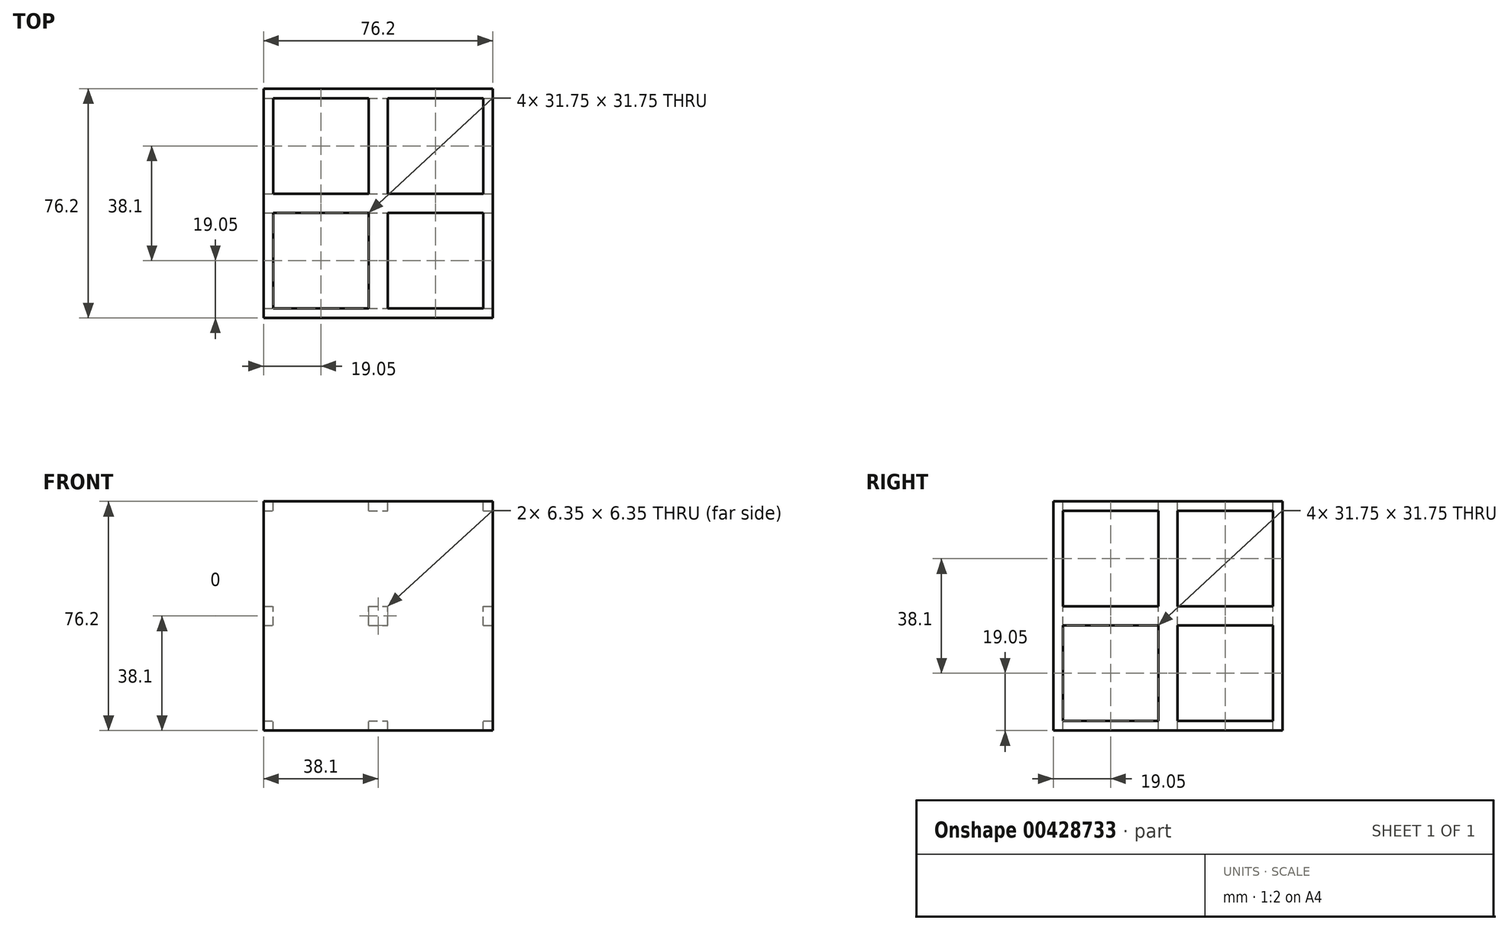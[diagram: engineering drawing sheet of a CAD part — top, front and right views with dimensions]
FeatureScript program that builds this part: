
annotation { "Feature Type Name" : "Feature", "Feature Type Description" : "" }
export const myFeature = defineFeature(function(context is Context, id is Id, definition is map)
    precondition{}
    {
        {
            var Q0;
            Q0=qCreatedBy(makeId("Top.planeOp"),FACE);
            var sketch = newSketch(context, id + "F0", { "sketchPlane" : qUnion([Q0])});
            skLineSegment(sketch, "E0.bottom", {"start": v(38.1, 38.1) * mm, "end": v(-38.1, 38.1) * mm});
            skLineSegment(sketch, "E0.top", {"start": v(38.1, -38.1) * mm, "end": v(-38.1, -38.1) * mm});
            skLineSegment(sketch, "E0.left", {"start": v(38.1, 38.1) * mm, "end": v(38.1, -38.1) * mm});
            skLineSegment(sketch, "E0.right", {"start": v(-38.1, 38.1) * mm, "end": v(-38.1, -38.1) * mm});
            skPoint(sketch, "E0.middle", {"position": v(0, 0) * mm});
            skSolve(sketch);
        }
        {
            var Q0;
            Q0 = qSketchRegion(id + "F0", true);
            extrude(context, id + "F1", {"entities" : qUnion([Q0]), "depth" : 76.2 * mm});
        }
        {
            var Q0;
            Q0=makeQuery(id+"F1.opExtrude","CAP_FACE",FACE,{"disambiguationData":[OSD([sQuery(id+"F0.wireOp",EDGE,"E0.bottom"),sQuery(id+"F0.wireOp",EDGE,"E0.top"),sQuery(id+"F0.wireOp",EDGE,"E0.left"),sQuery(id+"F0.wireOp",EDGE,"E0.right")])],"isStart":false});
            var sketch = newSketch(context, id + "F2", { "sketchPlane" : qUnion([Q0])});
            skLineSegment(sketch, "E1", {"start": v(-38.1, 38.1) * mm, "end": v(38.1, -38.1) * mm, "construction": true});
            skLineSegment(sketch, "E2", {"start": v(38.1, 38.1) * mm, "end": v(-38.1, -38.1) * mm, "construction": true});
            skLineSegment(sketch, "E3", {"start": v(-38.1, 0) * mm, "end": v(38.1, 0) * mm, "construction": true});
            skLineSegment(sketch, "E4", {"start": v(0, 38.1) * mm, "end": v(0, -38.1) * mm, "construction": true});
            skLineSegment(sketch, "E5", {"start": v(-38.1, 0) * mm, "end": v(0, 38.1) * mm, "construction": true});
            skLineSegment(sketch, "E6", {"start": v(-38.1, 0) * mm, "end": v(0, -38.1) * mm, "construction": true});
            skLineSegment(sketch, "E7", {"start": v(0, -38.1) * mm, "end": v(38.1, 0) * mm, "construction": true});
            skLineSegment(sketch, "E8", {"start": v(38.1, 0) * mm, "end": v(0, 38.1) * mm, "construction": true});
            skLineSegment(sketch, "E9", {"start": v(38.1, 19.05) * mm, "end": v(-38.1, 19.05) * mm, "construction": true});
            skPoint(sketch, "E9.startSnap0", {"position": v(19.05, 19.05) * mm});
            skPoint(sketch, "E9.endSnap0", {"position": v(-19.05, 19.05) * mm});
            skLineSegment(sketch, "E10", {"start": v(-38.1, -19.05) * mm, "end": v(38.1, -19.05) * mm, "construction": true});
            skPoint(sketch, "E10.startSnap0", {"position": v(-19.05, -19.05) * mm});
            skLineSegment(sketch, "E11.bottom", {"start": v(-3.18, 34.92) * mm, "end": v(-34.93, 34.92) * mm});
            skLineSegment(sketch, "E11.top", {"start": v(-3.18, 3.17) * mm, "end": v(-34.93, 3.17) * mm});
            skLineSegment(sketch, "E11.left", {"start": v(-3.18, 34.92) * mm, "end": v(-3.18, 3.17) * mm});
            skLineSegment(sketch, "E11.right", {"start": v(-34.93, 34.92) * mm, "end": v(-34.93, 3.17) * mm});
            skLineSegment(sketch, "E12.bottom", {"start": v(34.93, 34.92) * mm, "end": v(3.18, 34.92) * mm});
            skLineSegment(sketch, "E12.top", {"start": v(34.93, 3.18) * mm, "end": v(3.18, 3.17) * mm});
            skLineSegment(sketch, "E12.left", {"start": v(34.93, 34.92) * mm, "end": v(34.93, 3.18) * mm});
            skLineSegment(sketch, "E12.right", {"start": v(3.18, 34.92) * mm, "end": v(3.18, 3.18) * mm});
            skLineSegment(sketch, "E13.bottom", {"start": v(-3.17, -3.18) * mm, "end": v(-34.92, -3.17) * mm});
            skLineSegment(sketch, "E13.top", {"start": v(-3.17, -34.93) * mm, "end": v(-34.92, -34.93) * mm});
            skLineSegment(sketch, "E13.left", {"start": v(-3.17, -3.18) * mm, "end": v(-3.17, -34.93) * mm});
            skLineSegment(sketch, "E13.right", {"start": v(-34.92, -3.17) * mm, "end": v(-34.92, -34.93) * mm});
            skLineSegment(sketch, "E14.bottom", {"start": v(34.92, -3.18) * mm, "end": v(3.17, -3.18) * mm});
            skLineSegment(sketch, "E14.top", {"start": v(34.92, -34.92) * mm, "end": v(3.17, -34.92) * mm});
            skLineSegment(sketch, "E14.left", {"start": v(34.92, -3.18) * mm, "end": v(34.92, -34.92) * mm});
            skLineSegment(sketch, "E14.right", {"start": v(3.17, -3.18) * mm, "end": v(3.17, -34.92) * mm});
            skPoint(sketch, "E14.middle", {"position": v(19.05, -19.05) * mm});
            skLineSegment(sketch, "E15", {"start": v(-19.05, -34.93) * mm, "end": v(-19.05, -38.1) * mm, "construction": true});
            skLineSegment(sketch, "E16", {"start": v(-19.05, 3.17) * mm, "end": v(-19.05, -3.17) * mm, "construction": true});
            skSolve(sketch);
        }
        {
            var Q0;
            Q0=makeQuery(id+"F2.imprint","IMPRINT",FACE,{"disambiguationData":[TD([[makeQuery(id+"F2.imprint","IMPRINT",EDGE,{"derivedFrom":sQuery(id+"F2.wireOp",EDGE,"E11.bottom")}),1.0]])]});
            extrude(context, id + "F3", {"entities" : qUnion([Q0]), "operationType" : NewBodyOperationType.REMOVE, "oppositeDirection" : true, "depth" : 102.87 * mm});
        }
        {
            var Q0;
            Q0=makeQuery(id+"F2.imprint","IMPRINT",FACE,{"disambiguationData":[TD([[makeQuery(id+"F2.imprint","IMPRINT",EDGE,{"derivedFrom":sQuery(id+"F2.wireOp",EDGE,"E12.bottom")}),1.0]])]});
            extrude(context, id + "F4", {"entities" : qUnion([Q0]), "operationType" : NewBodyOperationType.REMOVE, "oppositeDirection" : true, "depth" : 134.87 * mm});
        }
        {
            var Q0;
            Q0=makeQuery(id+"F2.imprint","IMPRINT",FACE,{"disambiguationData":[TD([[makeQuery(id+"F2.imprint","IMPRINT",EDGE,{"derivedFrom":sQuery(id+"F2.wireOp",EDGE,"E13.bottom")}),1.0]])]});
            extrude(context, id + "F5", {"entities" : qUnion([Q0]), "operationType" : NewBodyOperationType.REMOVE, "oppositeDirection" : true, "depth" : 137.92 * mm});
        }
        {
            var Q0;
            Q0=makeQuery(id+"F2.imprint","IMPRINT",FACE,{"disambiguationData":[TD([[makeQuery(id+"F2.imprint","IMPRINT",EDGE,{"derivedFrom":sQuery(id+"F2.wireOp",EDGE,"E14.bottom")}),1.0]])]});
            extrude(context, id + "F6", {"entities" : qUnion([Q0]), "operationType" : NewBodyOperationType.REMOVE, "oppositeDirection" : true, "depth" : 121.4 * mm});
        }
        {
            var Q0;
            Q0=makeQuery(id+"F1.opExtrude","SWEPT_FACE",FACE,{"disambiguationData":[OSD([sQuery(id+"F0.wireOp",EDGE,"E0.left")])]});
            var sketch = newSketch(context, id + "F7", { "sketchPlane" : qUnion([Q0])});
            skLineSegment(sketch, "E17", {"start": v(-38.1, 76.2) * mm, "end": v(38.1, 0) * mm, "construction": true});
            skLineSegment(sketch, "E18", {"start": v(38.1, 76.2) * mm, "end": v(-38.1, 0) * mm, "construction": true});
            skLineSegment(sketch, "E19", {"start": v(-38.1, 38.1) * mm, "end": v(38.1, 38.1) * mm, "construction": true});
            skLineSegment(sketch, "E20", {"start": v(0, 76.2) * mm, "end": v(0, 0) * mm, "construction": true});
            skLineSegment(sketch, "E21", {"start": v(-38.1, 38.1) * mm, "end": v(0, 76.2) * mm, "construction": true});
            skLineSegment(sketch, "E22", {"start": v(0, 76.2) * mm, "end": v(38.1, 38.1) * mm, "construction": true});
            skLineSegment(sketch, "E23", {"start": v(38.1, 38.1) * mm, "end": v(0, 0) * mm, "construction": true});
            skLineSegment(sketch, "E24", {"start": v(-38.1, 38.1) * mm, "end": v(0, 0) * mm, "construction": true});
            skLineSegment(sketch, "E25", {"start": v(38.1, 19.05) * mm, "end": v(-38.1, 19.05) * mm, "construction": true});
            skPoint(sketch, "E25.startSnap0", {"position": v(19.05, 19.05) * mm});
            skLineSegment(sketch, "E26", {"start": v(-38.1, 57.15) * mm, "end": v(38.1, 57.15) * mm, "construction": true});
            skPoint(sketch, "E26.startSnap0", {"position": v(-19.05, 57.15) * mm});
            skLineSegment(sketch, "E27.bottom", {"start": v(-34.92, 41.28) * mm, "end": v(-3.17, 41.28) * mm});
            skLineSegment(sketch, "E27.top", {"start": v(-34.92, 73.03) * mm, "end": v(-3.17, 73.03) * mm});
            skLineSegment(sketch, "E27.left", {"start": v(-34.92, 41.28) * mm, "end": v(-34.92, 73.03) * mm});
            skLineSegment(sketch, "E27.right", {"start": v(-3.17, 41.28) * mm, "end": v(-3.17, 73.03) * mm});
            skLineSegment(sketch, "E28.bottom", {"start": v(3.18, 73.03) * mm, "end": v(34.93, 73.03) * mm});
            skLineSegment(sketch, "E28.top", {"start": v(3.17, 41.28) * mm, "end": v(34.93, 41.28) * mm});
            skLineSegment(sketch, "E28.left", {"start": v(3.18, 73.03) * mm, "end": v(3.17, 41.28) * mm});
            skLineSegment(sketch, "E28.right", {"start": v(34.93, 73.03) * mm, "end": v(34.92, 41.28) * mm});
            skPoint(sketch, "E28.middle", {"position": v(19.05, 57.15) * mm});
            skLineSegment(sketch, "E29.bottom", {"start": v(-34.92, 34.93) * mm, "end": v(-3.17, 34.93) * mm});
            skLineSegment(sketch, "E29.top", {"start": v(-34.93, 3.18) * mm, "end": v(-3.17, 3.18) * mm});
            skLineSegment(sketch, "E29.left", {"start": v(-34.92, 34.93) * mm, "end": v(-34.92, 3.18) * mm});
            skLineSegment(sketch, "E29.right", {"start": v(-3.17, 34.93) * mm, "end": v(-3.17, 3.18) * mm});
            skPoint(sketch, "E29.middle", {"position": v(-19.05, 19.05) * mm});
            skLineSegment(sketch, "E30.bottom", {"start": v(3.18, 34.93) * mm, "end": v(34.93, 34.93) * mm});
            skLineSegment(sketch, "E30.top", {"start": v(3.18, 3.18) * mm, "end": v(34.93, 3.18) * mm});
            skLineSegment(sketch, "E30.left", {"start": v(3.18, 34.93) * mm, "end": v(3.18, 3.18) * mm});
            skLineSegment(sketch, "E30.right", {"start": v(34.93, 34.93) * mm, "end": v(34.93, 3.18) * mm});
            skSolve(sketch);
        }
        {
            var Q0;
            Q0 = qSketchRegion(id + "F7", true);
            extrude(context, id + "F8", {"entities" : qUnion([Q0]), "operationType" : NewBodyOperationType.REMOVE, "oppositeDirection" : true, "depth" : 107.7 * mm});
        }
    });
